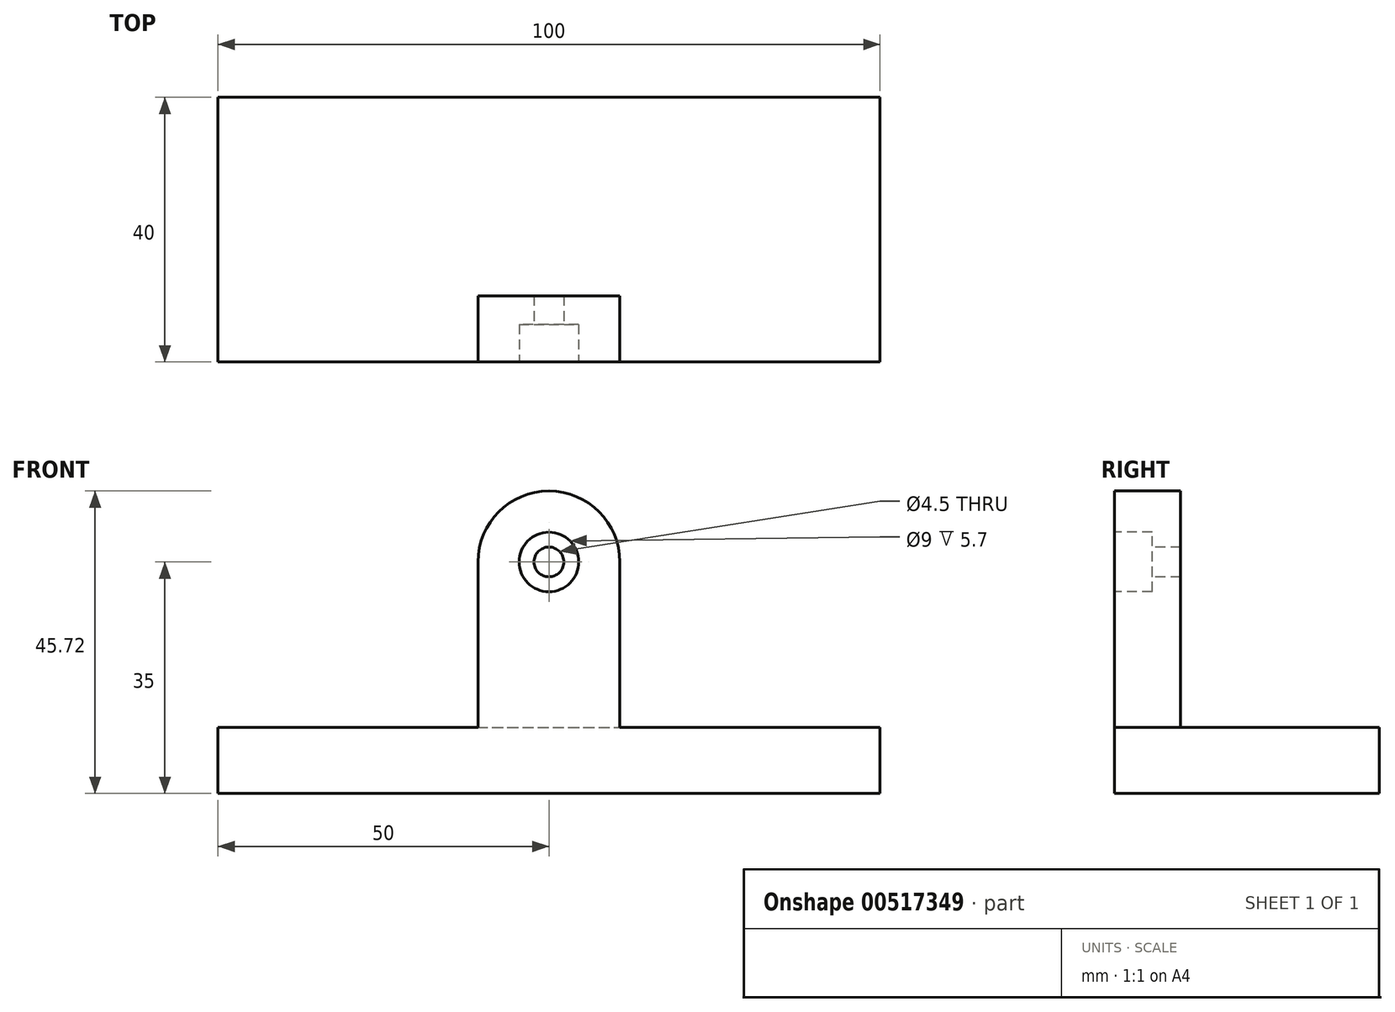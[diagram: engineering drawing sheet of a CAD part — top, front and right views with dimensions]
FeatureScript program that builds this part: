
annotation { "Feature Type Name" : "Feature", "Feature Type Description" : "" }
export const myFeature = defineFeature(function(context is Context, id is Id, definition is map)
    precondition{}
    {
        {
            var Q0;
            Q0=qCreatedBy(makeId("Top.planeOp"),FACE);
            var sketch = newSketch(context, id + "F0", { "sketchPlane" : qUnion([Q0])});
            skLineSegment(sketch, "E0.bottom", {"start": v(0, 0) * mm, "end": v(100, 0) * mm});
            skLineSegment(sketch, "E0.top", {"start": v(0, 40) * mm, "end": v(100, 40) * mm});
            skLineSegment(sketch, "E0.left", {"start": v(0, 0) * mm, "end": v(0, 40) * mm});
            skLineSegment(sketch, "E0.right", {"start": v(100, 0) * mm, "end": v(100, 40) * mm});
            skSolve(sketch);
        }
        {
            var Q0;
            Q0 = qSketchRegion(id + "F0", true);
            extrude(context, id + "F1", {"entities" : qUnion([Q0]), "depth" : 10 * mm, "offsetDistance" : 25 * mm});
        }
        {
            var Q0;
            Q0=makeQuery(id+"F1.opExtrude","SWEPT_FACE",FACE,{"disambiguationData":[OSD([sQuery(id+"F0.wireOp",EDGE,"E0.bottom")])]});
            var sketch = newSketch(context, id + "F2", { "sketchPlane" : qUnion([Q0])});
            skLineSegment(sketch, "E1", {"start": v(39.28, 0) * mm, "end": v(39.28, 35) * mm});
            skArc(sketch, "E2", {"start": v(39.28, 35) * mm, "mid": v(50, 45.72) * mm, "end": v(60.72, 35) * mm});
            skLineSegment(sketch, "E3", {"start": v(60.72, 35) * mm, "end": v(60.72, 0) * mm});
            skLineSegment(sketch, "E4", {"start": v(60.72, 0) * mm, "end": v(39.28, 0) * mm});
            skSolve(sketch);
        }
        {
            var Q0;
            Q0 = qSketchRegion(id + "F2", true);
            extrude(context, id + "F3", {"entities" : qUnion([Q0]), "operationType" : NewBodyOperationType.ADD, "oppositeDirection" : true, "depth" : 10 * mm, "offsetDistance" : 25 * mm});
        }
        {
            var Q0;
            Q0=makeQuery(id+"F3.boolean.opBoolean","MERGE",FACE,{"derivedFrom":[makeQuery(id+"F1.opExtrude","SWEPT_FACE",FACE,{"disambiguationData":[OSD([sQuery(id+"F0.wireOp",EDGE,"E0.bottom")])]}),makeQuery(id+"F3.opExtrude","CAP_FACE",FACE,{"disambiguationData":[OSD([sQuery(id+"F2.wireOp",EDGE,"E1"),sQuery(id+"F2.wireOp",EDGE,"E2"),sQuery(id+"F2.wireOp",EDGE,"E3"),sQuery(id+"F2.wireOp",EDGE,"E4")])],"isStart":true})]});
            var sketch = newSketch(context, id + "F4", { "sketchPlane" : qUnion([Q0])});
            skCircle(sketch, "E5", {"center": v(50, 35) * mm, "radius": 2.25 * mm});
            skSolve(sketch);
        }
        {
            var Q0;
            Q0=makeQuery(id+"F4.imprint","IMPRINT",FACE,{"disambiguationData":[TD([[makeQuery(id+"F4.imprint","IMPRINT",EDGE,{"derivedFrom":sQuery(id+"F4.wireOp",EDGE,"E5")}),1.0]])]});
            extrude(context, id + "F5", {"entities" : qUnion([Q0]), "operationType" : NewBodyOperationType.REMOVE, "endBound" : BoundingType.THROUGH_ALL, "oppositeDirection" : true, "depth" : 25 * mm, "offsetDistance" : 25 * mm});
        }
        {
            var Q0;
            Q0=makeQuery(id+"F3.boolean.opBoolean","MERGE",FACE,{"derivedFrom":[makeQuery(id+"F1.opExtrude","SWEPT_FACE",FACE,{"disambiguationData":[OSD([sQuery(id+"F0.wireOp",EDGE,"E0.bottom")])]}),makeQuery(id+"F3.opExtrude","CAP_FACE",FACE,{"disambiguationData":[OSD([sQuery(id+"F2.wireOp",EDGE,"E1"),sQuery(id+"F2.wireOp",EDGE,"E2"),sQuery(id+"F2.wireOp",EDGE,"E3"),sQuery(id+"F2.wireOp",EDGE,"E4")])],"isStart":true})]});
            var sketch = newSketch(context, id + "F6", { "sketchPlane" : qUnion([Q0])});
            skCircle(sketch, "E6", {"center": v(50, 35) * mm, "radius": 4.5 * mm});
            skSolve(sketch);
        }
        {
            var Q0;
            Q0 = qSketchRegion(id + "F6", true);
            extrude(context, id + "F7", {"entities" : qUnion([Q0]), "operationType" : NewBodyOperationType.REMOVE, "oppositeDirection" : true, "depth" : 5.7 * mm, "offsetDistance" : 25 * mm});
        }
    });
